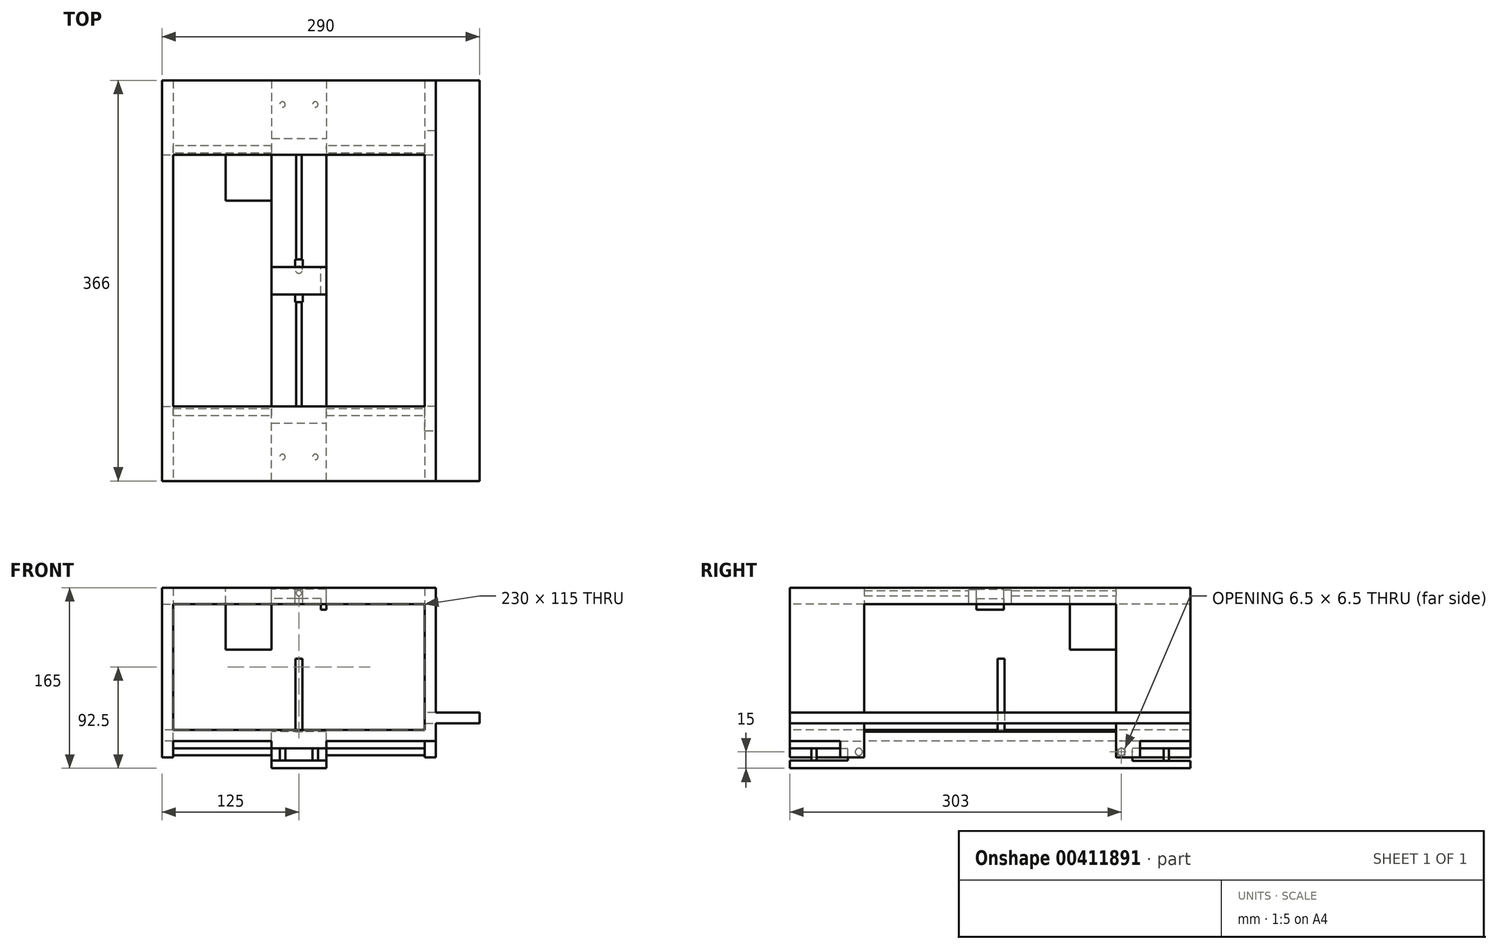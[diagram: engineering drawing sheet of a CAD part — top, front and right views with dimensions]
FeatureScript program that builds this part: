
annotation { "Feature Type Name" : "Feature", "Feature Type Description" : "" }
export const myFeature = defineFeature(function(context is Context, id is Id, definition is map)
    precondition{}
    {
        {
            var Q0;
            Q0=qCreatedBy(makeId("Top.planeOp"),FACE);
            var sketch = newSketch(context, id + "F0", { "sketchPlane" : qUnion([Q0])});
            skLineSegment(sketch, "E0.bottom", {"start": v(-125, 125) * mm, "end": v(125, 125) * mm});
            skLineSegment(sketch, "E0.top", {"start": v(-125, -125) * mm, "end": v(125, -125) * mm});
            skLineSegment(sketch, "E0.left", {"start": v(-125, 125) * mm, "end": v(-125, -125) * mm});
            skLineSegment(sketch, "E0.right", {"start": v(125, 125) * mm, "end": v(125, -125) * mm});
            skSolve(sketch);
        }
        {
            var Q0;
            Q0 = qSketchRegion(id + "F0", true);
            extrude(context, id + "F1", {"entities" : qUnion([Q0]), "endBound" : BoundingType.SYMMETRIC, "depth" : 140 * mm});
        }
        {
            var Q0;
            Q0=makeQuery(id+"F1.opExtrude","CAP_FACE",FACE,{"disambiguationData":[OSD([sQuery(id+"F0.wireOp",EDGE,"E0.bottom"),sQuery(id+"F0.wireOp",EDGE,"E0.top"),sQuery(id+"F0.wireOp",EDGE,"E0.left"),sQuery(id+"F0.wireOp",EDGE,"E0.right")])],"isStart":false});
            shell(context, id + "F2", {"entities" : qUnion([Q0]), "thickness" : 10 * mm});
        }
        {
            var Q0;
            Q0=makeQuery(id+"F1.opExtrude","SWEPT_FACE",FACE,{"disambiguationData":[OSD([sQuery(id+"F0.wireOp",EDGE,"E0.top")])]});
            var sketch = newSketch(context, id + "F3", { "sketchPlane" : qUnion([Q0])});
            skLineSegment(sketch, "E1.bottom", {"start": v(-115, 60) * mm, "end": v(115, 60) * mm});
            skLineSegment(sketch, "E1.top", {"start": v(-115, -60) * mm, "end": v(115, -60) * mm});
            skLineSegment(sketch, "E1.left", {"start": v(-115, 60) * mm, "end": v(-115, -60) * mm});
            skLineSegment(sketch, "E1.right", {"start": v(115, 60) * mm, "end": v(115, -60) * mm});
            skSolve(sketch);
        }
        {
            var Q0;
            Q0=makeQuery(id+"F3.imprint","IMPRINT",FACE,{"disambiguationData":[TD([[makeQuery(id+"F3.imprint","IMPRINT",EDGE,{"derivedFrom":sQuery(id+"F3.wireOp",EDGE,"E1.bottom")}),-1.0]])]});
            extrude(context, id + "F4", {"entities" : qUnion([Q0]), "operationType" : NewBodyOperationType.REMOVE, "oppositeDirection" : true, "depth" : 300 * mm});
        }
        {
            var Q0;
            Q0=makeQuery(id+"F1.opExtrude","SWEPT_FACE",FACE,{"disambiguationData":[OSD([sQuery(id+"F0.wireOp",EDGE,"E0.left")])]});
            var sketch = newSketch(context, id + "F5", { "sketchPlane" : qUnion([Q0])});
            skLineSegment(sketch, "E2.bottom", {"start": v(115, 60) * mm, "end": v(-115, 60) * mm});
            skLineSegment(sketch, "E2.top", {"start": v(115, -60) * mm, "end": v(-115, -60) * mm});
            skLineSegment(sketch, "E2.left", {"start": v(115, 60) * mm, "end": v(115, -60) * mm});
            skLineSegment(sketch, "E2.right", {"start": v(-115, 60) * mm, "end": v(-115, -60) * mm});
            skSolve(sketch);
        }
        {
            var Q0;
            Q0=makeQuery(id+"F5.imprint","IMPRINT",FACE,{"disambiguationData":[TD([[makeQuery(id+"F5.imprint","IMPRINT",EDGE,{"derivedFrom":sQuery(id+"F5.wireOp",EDGE,"E2.bottom")}),1.0]])]});
            extrude(context, id + "F6", {"entities" : qUnion([Q0]), "operationType" : NewBodyOperationType.REMOVE, "oppositeDirection" : true, "depth" : 300 * mm});
        }
        {
            var Q0;
            Q0=makeQuery(id+"F6.boolean.opBoolean","MERGE",FACE,{"derivedFrom":[makeQuery(id+"F4.boolean.opBoolean","MERGE",FACE,{"derivedFrom":[makeQuery(id+"F2.opShell","OFFSET_FACE",FACE,{"disambiguationData":[OSD([sQuery(id+"F0.wireOp",EDGE,"E0.bottom"),sQuery(id+"F0.wireOp",EDGE,"E0.top"),sQuery(id+"F0.wireOp",EDGE,"E0.left"),sQuery(id+"F0.wireOp",EDGE,"E0.right")])]}),makeQuery(id+"F4.opExtrude","SWEPT_FACE",FACE,{"disambiguationData":[OSD([sQuery(id+"F3.wireOp",EDGE,"E1.top")])]})]}),makeQuery(id+"F6.opExtrude","SWEPT_FACE",FACE,{"disambiguationData":[OSD([sQuery(id+"F5.wireOp",EDGE,"E2.top")])]})]});
            var sketch = newSketch(context, id + "F7", { "sketchPlane" : qUnion([Q0])});
            skLineSegment(sketch, "E3.bottom", {"start": v(-115, 115) * mm, "end": v(115, 115) * mm});
            skLineSegment(sketch, "E3.top", {"start": v(-115, -115) * mm, "end": v(115, -115) * mm});
            skLineSegment(sketch, "E3.left", {"start": v(-115, 115) * mm, "end": v(-115, -115) * mm});
            skLineSegment(sketch, "E3.right", {"start": v(115, 115) * mm, "end": v(115, -115) * mm});
            skSolve(sketch);
        }
        {
            var Q0;
            Q0=makeQuery(id+"F7.imprint","IMPRINT",FACE,{"disambiguationData":[TD([[makeQuery(id+"F7.imprint","IMPRINT",EDGE,{"derivedFrom":sQuery(id+"F7.wireOp",EDGE,"E3.bottom")}),-1.0]])]});
            extrude(context, id + "F8", {"entities" : qUnion([Q0]), "operationType" : NewBodyOperationType.REMOVE, "oppositeDirection" : true, "depth" : 500 * mm});
        }
        {
            var Q0;
            Q0=makeQuery(id+"F1.opExtrude","CAP_FACE",FACE,{"disambiguationData":[OSD([sQuery(id+"F0.wireOp",EDGE,"E0.bottom"),sQuery(id+"F0.wireOp",EDGE,"E0.top"),sQuery(id+"F0.wireOp",EDGE,"E0.left"),sQuery(id+"F0.wireOp",EDGE,"E0.right")])],"isStart":true});
            var sketch = newSketch(context, id + "F9", { "sketchPlane" : qUnion([Q0])});
            skLineSegment(sketch, "E4.bottom", {"start": v(-125, -125) * mm, "end": v(-115, -125) * mm});
            skLineSegment(sketch, "E4.top", {"start": v(-125, -115) * mm, "end": v(-115, -115) * mm});
            skLineSegment(sketch, "E4.left", {"start": v(-125, -125) * mm, "end": v(-125, -115) * mm});
            skLineSegment(sketch, "E4.right", {"start": v(-115, -125) * mm, "end": v(-115, -115) * mm});
            skLineSegment(sketch, "E5.bottom", {"start": v(-115, 115) * mm, "end": v(-125, 115) * mm});
            skLineSegment(sketch, "E5.top", {"start": v(-115, 125) * mm, "end": v(-125, 125) * mm});
            skLineSegment(sketch, "E5.left", {"start": v(-115, 115) * mm, "end": v(-115, 125) * mm});
            skLineSegment(sketch, "E5.right", {"start": v(-125, 115) * mm, "end": v(-125, 125) * mm});
            skLineSegment(sketch, "E6.bottom", {"start": v(125, -125) * mm, "end": v(115, -125) * mm});
            skLineSegment(sketch, "E6.top", {"start": v(125, -115) * mm, "end": v(115, -115) * mm});
            skLineSegment(sketch, "E6.left", {"start": v(125, -125) * mm, "end": v(125, -115) * mm});
            skLineSegment(sketch, "E6.right", {"start": v(115, -125) * mm, "end": v(115, -115) * mm});
            skLineSegment(sketch, "E7.bottom", {"start": v(125, 125) * mm, "end": v(115, 125) * mm});
            skLineSegment(sketch, "E7.top", {"start": v(125, 115) * mm, "end": v(115, 115) * mm});
            skLineSegment(sketch, "E7.left", {"start": v(125, 125) * mm, "end": v(125, 115) * mm});
            skLineSegment(sketch, "E7.right", {"start": v(115, 125) * mm, "end": v(115, 115) * mm});
            skSolve(sketch);
        }
        {
            var Q0;
            Q0 = qSketchRegion(id + "F9", true);
            var Q1;
            Q1=makeQuery(id+"F1.opExtrude","CAP_FACE",FACE,{"disambiguationData":[OSD([sQuery(id+"F0.wireOp",EDGE,"E0.bottom"),sQuery(id+"F0.wireOp",EDGE,"E0.top"),sQuery(id+"F0.wireOp",EDGE,"E0.left"),sQuery(id+"F0.wireOp",EDGE,"E0.right")])],"isStart":false});
            extrude(context, id + "F10", {"entities" : qUnion([Q0, Q1]), "operationType" : NewBodyOperationType.ADD, "depth" : 15 * mm});
        }
        {
            var Q0;
            Q0=makeQuery(id+"F10.boolean.opBoolean","MERGE",FACE,{"derivedFrom":[makeQuery(id+"F1.opExtrude","SWEPT_FACE",FACE,{"disambiguationData":[OSD([sQuery(id+"F0.wireOp",EDGE,"E0.bottom")])]}),makeQuery(id+"F10.opExtrude","SWEPT_FACE",FACE,{"disambiguationData":[OSD([sQuery(id+"F9.wireOp",EDGE,"E4.bottom")])]}),makeQuery(id+"F10.opExtrude","SWEPT_FACE",FACE,{"disambiguationData":[OSD([sQuery(id+"F9.wireOp",EDGE,"E6.bottom")])]})]});
            var sketch = newSketch(context, id + "F11", { "sketchPlane" : qUnion([Q0])});
            skCircle(sketch, "E8", {"center": v(0, 65) * mm, "radius": 2.5 * mm});
            skSolve(sketch);
        }
        {
            var Q0;
            Q0 = qSketchRegion(id + "F11", true);
            extrude(context, id + "F12", {"entities" : qUnion([Q0]), "operationType" : NewBodyOperationType.ADD, "oppositeDirection" : true, "depth" : 250 * mm});
        }
        {
            var Q0;
            Q0=qCreatedBy(makeId("Front.planeOp"),FACE);
            var sketch = newSketch(context, id + "F13", { "sketchPlane" : qUnion([Q0])});
            skLineSegment(sketch, "E9.bottom", {"start": v(25, 50) * mm, "end": v(-25, 50) * mm});
            skLineSegment(sketch, "E9.top", {"start": v(25, 68.5) * mm, "end": v(-25, 68.5) * mm});
            skLineSegment(sketch, "E9.left", {"start": v(25, 50) * mm, "end": v(25, 68.5) * mm});
            skLineSegment(sketch, "E9.right", {"start": v(-25, 50) * mm, "end": v(-25, 68.5) * mm});
            skSolve(sketch);
        }
        {
            var Q0;
            Q0 = qSketchRegion(id + "F13", true);
            extrude(context, id + "F14", {"entities" : qUnion([Q0]), "operationType" : NewBodyOperationType.ADD, "endBound" : BoundingType.SYMMETRIC, "depth" : 25 * mm});
        }
        {
            var Q0;
            Q0=makeQuery(id+"F14.opExtrude","SWEPT_FACE",FACE,{"disambiguationData":[OSD([sQuery(id+"F13.wireOp",EDGE,"E9.bottom")])]});
            var sketch = newSketch(context, id + "F15", { "sketchPlane" : qUnion([Q0])});
            skLineSegment(sketch, "E10.right", {"start": v(20, 7.5) * mm, "end": v(20, -12.5) * mm});
            skLineSegment(sketch, "E11", {"start": v(20, 7.5) * mm, "end": v(20, 12.5) * mm});
            skLineSegment(sketch, "E12", {"start": v(20, 12.5) * mm, "end": v(25, 12.5) * mm});
            skLineSegment(sketch, "E13", {"start": v(25, 12.5) * mm, "end": v(25, -12.5) * mm});
            skLineSegment(sketch, "E14", {"start": v(25, -12.5) * mm, "end": v(20, -12.5) * mm});
            skSolve(sketch);
        }
        {
            var Q0;
            {var subQ3=sQuery(id+"F15.wireOp",EDGE,"E10.right");Q0=makeQuery(id+"F15.imprint","IMPRINT",FACE,{"disambiguationData":[TD([[makeQuery(id+"F15.imprint","IMPRINT",EDGE,{"derivedFrom":subQ3}),-1.0]])]});}
            extrude(context, id + "F16", {"entities" : qUnion([Q0]), "operationType" : NewBodyOperationType.REMOVE, "oppositeDirection" : true, "depth" : 10 * mm});
        }
        {
            var Q0;
            Q0=qCreatedBy(makeId("Right.planeOp"),FACE);
            var sketch = newSketch(context, id + "F17", { "sketchPlane" : qUnion([Q0])});
            skLineSegment(sketch, "E15.bottom", {"start": v(-12.5, 55) * mm, "end": v(-19.5, 55) * mm});
            skLineSegment(sketch, "E15.top", {"start": v(-12.5, 68) * mm, "end": v(-19.5, 68) * mm});
            skLineSegment(sketch, "E15.left", {"start": v(-12.5, 55) * mm, "end": v(-12.5, 68) * mm});
            skLineSegment(sketch, "E15.right", {"start": v(-19.5, 55) * mm, "end": v(-19.5, 68) * mm});
            skLineSegment(sketch, "E16.bottom", {"start": v(12.5, 55) * mm, "end": v(19.5, 55) * mm});
            skLineSegment(sketch, "E16.top", {"start": v(12.5, 68) * mm, "end": v(19.5, 68) * mm});
            skLineSegment(sketch, "E16.left", {"start": v(12.5, 55) * mm, "end": v(12.5, 68) * mm});
            skLineSegment(sketch, "E16.right", {"start": v(19.5, 55) * mm, "end": v(19.5, 68) * mm});
            skSolve(sketch);
        }
        {
            var Q0;
            Q0 = qSketchRegion(id + "F17", true);
            extrude(context, id + "F18", {"entities" : qUnion([Q0]), "operationType" : NewBodyOperationType.ADD, "endBound" : BoundingType.SYMMETRIC, "depth" : 7 * mm});
        }
        {
            var Q0;
            Q0=makeQuery(id+"F10.opExtrude","SWEPT_FACE",FACE,{"disambiguationData":[OSD([sQuery(id+"F9.wireOp",EDGE,"E4.right")])]});
            var sketch = newSketch(context, id + "F19", { "sketchPlane" : qUnion([Q0])});
            skCircle(sketch, "E17", {"center": v(120, -80) * mm, "radius": 3.25 * mm});
            skSolve(sketch);
        }
        {
            var Q0;
            Q0 = qSketchRegion(id + "F19", true);
            extrude(context, id + "F20", {"entities" : qUnion([Q0]), "operationType" : NewBodyOperationType.ADD, "depth" : 240 * mm});
        }
        {
            var Q0;
            Q0=qCreatedBy(makeId("Front.planeOp"),FACE);
            var sketch = newSketch(context, id + "F21", { "sketchPlane" : qUnion([Q0])});
            skLineSegment(sketch, "E18.bottom", {"start": v(25, -95) * mm, "end": v(-25, -95) * mm});
            skLineSegment(sketch, "E18.top", {"start": v(25, -61.69) * mm, "end": v(-25, -61.69) * mm});
            skLineSegment(sketch, "E18.left", {"start": v(25, -95) * mm, "end": v(25, -61.69) * mm});
            skLineSegment(sketch, "E18.right", {"start": v(-25, -95) * mm, "end": v(-25, -61.69) * mm});
            skSolve(sketch);
        }
        {
            var Q0;
            Q0=makeQuery(id+"F21.imprint","IMPRINT",FACE,{"disambiguationData":[TD([[makeQuery(id+"F21.imprint","IMPRINT",EDGE,{"derivedFrom":sQuery(id+"F21.wireOp",EDGE,"E18.bottom")}),-1.0]])]});
            extrude(context, id + "F22", {"entities" : qUnion([Q0]), "operationType" : NewBodyOperationType.ADD, "endBound" : BoundingType.SYMMETRIC, "depth" : 230 * mm});
        }
        {
            var Q0;
            Q0=makeQuery(id+"F10.opExtrude","SWEPT_FACE",FACE,{"disambiguationData":[OSD([sQuery(id+"F9.wireOp",EDGE,"E7.right")])]});
            var sketch = newSketch(context, id + "F23", { "sketchPlane" : qUnion([Q0])});
            skCircle(sketch, "E19", {"center": v(120, -80) * mm, "radius": 3.25 * mm});
            skSolve(sketch);
        }
        {
            var Q0;
            Q0=makeQuery(id+"F23.imprint","IMPRINT",FACE,{"disambiguationData":[TD([[makeQuery(id+"F23.imprint","IMPRINT",EDGE,{"derivedFrom":sQuery(id+"F23.wireOp",EDGE,"E19")}),1.0]])]});
            extrude(context, id + "F24", {"entities" : qUnion([Q0]), "operationType" : NewBodyOperationType.ADD, "depth" : 240 * mm});
        }
        {
            var Q0;
            Q0=makeQuery(id+"F22.opExtrude","SWEPT_FACE",FACE,{"disambiguationData":[OSD([sQuery(id+"F21.wireOp",EDGE,"E18.bottom")])]});
            var sketch = newSketch(context, id + "F25", { "sketchPlane" : qUnion([Q0])});
            skCircle(sketch, "E20", {"center": v(0, -10) * mm, "radius": 3.25 * mm});
            skSolve(sketch);
        }
        {
            var Q0;
            Q0=makeQuery(id+"F25.imprint","IMPRINT",FACE,{"disambiguationData":[TD([[makeQuery(id+"F25.imprint","IMPRINT",EDGE,{"derivedFrom":sQuery(id+"F25.wireOp",EDGE,"E20")}),1.0]])]});
            extrude(context, id + "F26", {"entities" : qUnion([Q0]), "operationType" : NewBodyOperationType.ADD, "oppositeDirection" : true, "depth" : 100 * mm});
        }
        {
            var Q0;
            Q0=makeQuery(id+"F1.opExtrude","CAP_FACE",FACE,{"disambiguationData":[OSD([sQuery(id+"F0.wireOp",EDGE,"E0.bottom"),sQuery(id+"F0.wireOp",EDGE,"E0.top"),sQuery(id+"F0.wireOp",EDGE,"E0.left"),sQuery(id+"F0.wireOp",EDGE,"E0.right")])],"isStart":false});
            var sketch = newSketch(context, id + "F27", { "sketchPlane" : qUnion([Q0])});
            skLineSegment(sketch, "E21.0", {"start": v(-25, -12.5) * mm, "end": v(-25, 12.5) * mm});
            skLineSegment(sketch, "E22.0", {"start": v(-25, -115) * mm, "end": v(-25, 115) * mm});
            skLineSegment(sketch, "E23.bottom", {"start": v(-25, 115) * mm, "end": v(-67, 115) * mm});
            skLineSegment(sketch, "E23.top", {"start": v(-25, 73) * mm, "end": v(-67, 73) * mm});
            skLineSegment(sketch, "E23.left", {"start": v(-25, 115) * mm, "end": v(-25, 73) * mm});
            skLineSegment(sketch, "E23.right", {"start": v(-67, 115) * mm, "end": v(-67, 73) * mm});
            skSolve(sketch);
        }
        {
            var Q0;
            Q0=makeQuery(id+"F27.imprint","IMPRINT",FACE,{"disambiguationData":[TD([[makeQuery(id+"F27.imprint","IMPRINT",EDGE,{"derivedFrom":sQuery(id+"F27.wireOp",EDGE,"E23.bottom")}),-1.0]])]});
            extrude(context, id + "F28", {"entities" : qUnion([Q0]), "oppositeDirection" : true, "depth" : 56.5 * mm});
        }
        {
            var Q0;
            {var subQ0=sQuery(id+"F0.wireOp",EDGE,"E0.bottom");Q0=makeQuery(id+"F10.boolean.opBoolean","MERGE",FACE,{"derivedFrom":[makeQuery(id+"F1.opExtrude","SWEPT_FACE",FACE,{"disambiguationData":[OSD([subQ0])]}),makeQuery(id+"F10.opExtrude","SWEPT_FACE",FACE,{"disambiguationData":[OSD([subQ0]),TDD([makeQuery(id+"F1.opExtrude","CAP_EDGE",EDGE,{"disambiguationData":[OSD([subQ0])],"isStart":false})])]}),makeQuery(id+"F10.opExtrude","SWEPT_FACE",FACE,{"disambiguationData":[OSD([sQuery(id+"F9.wireOp",EDGE,"E4.bottom")])]}),makeQuery(id+"F10.opExtrude","SWEPT_FACE",FACE,{"disambiguationData":[OSD([sQuery(id+"F9.wireOp",EDGE,"E6.bottom")])]})]});}
            var sketch = newSketch(context, id + "F29", { "sketchPlane" : qUnion([Q0])});
            skLineSegment(sketch, "E24.0.0", {"start": v(-115, -70) * mm, "end": v(115, -70) * mm});
            skLineSegment(sketch, "E24.0.1", {"start": v(115, -70) * mm, "end": v(115, -85) * mm});
            skLineSegment(sketch, "E24.0.2", {"start": v(115, -85) * mm, "end": v(125, -85) * mm});
            skLineSegment(sketch, "E24.0.3", {"start": v(125, -85) * mm, "end": v(125, 70) * mm});
            skLineSegment(sketch, "E24.0.4", {"start": v(125, 70) * mm, "end": v(-125, 70) * mm});
            skLineSegment(sketch, "E24.0.5", {"start": v(-125, 70) * mm, "end": v(-125, -85) * mm});
            skLineSegment(sketch, "E24.0.6", {"start": v(-125, -85) * mm, "end": v(-115, -85) * mm});
            skLineSegment(sketch, "E24.0.7", {"start": v(-115, -85) * mm, "end": v(-115, -70) * mm});
            skSolve(sketch);
        }
        {
            var Q0;
            Q0=makeQuery(id+"F29.imprint","IMPRINT",FACE,{"disambiguationData":[TD([[makeQuery(id+"F29.imprint","IMPRINT",EDGE,{"derivedFrom":sQuery(id+"F29.wireOp",EDGE,"E24.0.0")}),-1.0]])]});
            extrude(context, id + "F30", {"entities" : qUnion([Q0]), "operationType" : NewBodyOperationType.ADD, "depth" : 58 * mm});
        }
        {
            var Q0;
            {var subQ0=sQuery(id+"F0.wireOp",EDGE,"E0.top");Q0=makeQuery(id+"F10.boolean.opBoolean","MERGE",FACE,{"derivedFrom":[makeQuery(id+"F1.opExtrude","SWEPT_FACE",FACE,{"disambiguationData":[OSD([subQ0])]}),makeQuery(id+"F10.opExtrude","SWEPT_FACE",FACE,{"disambiguationData":[OSD([subQ0]),TDD([makeQuery(id+"F1.opExtrude","CAP_EDGE",EDGE,{"disambiguationData":[OSD([subQ0])],"isStart":false})])]}),makeQuery(id+"F10.opExtrude","SWEPT_FACE",FACE,{"disambiguationData":[OSD([sQuery(id+"F9.wireOp",EDGE,"E5.top")])]}),makeQuery(id+"F10.opExtrude","SWEPT_FACE",FACE,{"disambiguationData":[OSD([sQuery(id+"F9.wireOp",EDGE,"E7.bottom")])]})]});}
            var sketch = newSketch(context, id + "F31", { "sketchPlane" : qUnion([Q0])});
            skPoint(sketch, "E25.0", {"position": v(115, -70) * mm});
            skPoint(sketch, "E25.1", {"position": v(115, -60) * mm});
            skSolve(sketch);
        }
        {
            var Q0;
            {var subQ0=sQuery(id+"F0.wireOp",EDGE,"E0.top");var subQ3=makeQuery(id+"F1.opExtrude","CAP_EDGE",EDGE,{"disambiguationData":[OSD([subQ0])],"isStart":false});Q0=makeQuery(id+"F31.imprint","IMPRINT",FACE,{"disambiguationData":[TD([[makeQuery(id+"F31.imprint","IMPRINT",EDGE,{"derivedFrom":subQ3}),-1.0]])]});}
            extrude(context, id + "F32", {"entities" : qUnion([Q0]), "operationType" : NewBodyOperationType.ADD, "depth" : 58 * mm});
        }
        {
            var Q0;
            {var subQ0=sQuery(id+"F21.wireOp",EDGE,"E18.bottom");var subQ1=sQuery(id+"F21.wireOp",EDGE,"E18.left");var subQ2=sQuery(id+"F21.wireOp",EDGE,"E18.right");Q0=makeQuery(id+"F22.boolean.opBoolean","SPLIT",FACE,{"disambiguationData":[TD([makeQuery(id+"F22.opExtrude","SWEPT_FACE",FACE,{"disambiguationData":[OSD([subQ0])]})])],"derivedFrom":makeQuery(id+"F22.opExtrude","CAP_FACE",FACE,{"disambiguationData":[OSD([subQ0,sQuery(id+"F21.wireOp",EDGE,"E18.top"),subQ1,subQ2])],"isStart":true})});}
            var sketch = newSketch(context, id + "F33", { "sketchPlane" : qUnion([Q0])});
            skLineSegment(sketch, "E26.0.0", {"start": v(25, -95) * mm, "end": v(25, -70) * mm});
            skLineSegment(sketch, "E26.0.1", {"start": v(25, -70) * mm, "end": v(-25, -70) * mm});
            skLineSegment(sketch, "E26.0.2", {"start": v(-25, -70) * mm, "end": v(-25, -95) * mm});
            skLineSegment(sketch, "E26.0.3", {"start": v(-25, -95) * mm, "end": v(25, -95) * mm});
            skSolve(sketch);
        }
        {
            var Q0;
            Q0 = qSketchRegion(id + "F33", true);
            extrude(context, id + "F34", {"entities" : qUnion([Q0]), "operationType" : NewBodyOperationType.ADD, "depth" : 15 * mm});
        }
        {
            var Q0;
            Q0=makeQuery(id+"F34.opExtrude","CAP_FACE",FACE,{"disambiguationData":[OSD([sQuery(id+"F33.wireOp",EDGE,"E26.0.0"),sQuery(id+"F33.wireOp",EDGE,"E26.0.1"),sQuery(id+"F33.wireOp",EDGE,"E26.0.2"),sQuery(id+"F33.wireOp",EDGE,"E26.0.3")])],"isStart":false});
            var sketch = newSketch(context, id + "F35", { "sketchPlane" : qUnion([Q0])});
            skLineSegment(sketch, "E27.bottom", {"start": v(25, -95) * mm, "end": v(-25, -95) * mm});
            skLineSegment(sketch, "E27.top", {"start": v(25, -88.07) * mm, "end": v(-25, -88.07) * mm});
            skLineSegment(sketch, "E27.left", {"start": v(25, -95) * mm, "end": v(25, -88.07) * mm});
            skLineSegment(sketch, "E27.right", {"start": v(-25, -95) * mm, "end": v(-25, -88.07) * mm});
            skLineSegment(sketch, "E28.bottom", {"start": v(25, -70) * mm, "end": v(-25, -70) * mm});
            skLineSegment(sketch, "E28.top", {"start": v(25, -76.65) * mm, "end": v(-25, -76.65) * mm});
            skLineSegment(sketch, "E28.left", {"start": v(25, -70) * mm, "end": v(25, -76.65) * mm});
            skLineSegment(sketch, "E28.right", {"start": v(-25, -70) * mm, "end": v(-25, -76.65) * mm});
            skSolve(sketch);
        }
        {
            var Q0;
            Q0=makeQuery(id+"F35.imprint","IMPRINT",FACE,{"disambiguationData":[TD([[makeQuery(id+"F35.imprint","IMPRINT",EDGE,{"derivedFrom":sQuery(id+"F35.wireOp",EDGE,"E27.bottom")}),1.0]])]});
            var Q1;
            Q1=makeQuery(id+"F35.imprint","IMPRINT",FACE,{"disambiguationData":[TD([[makeQuery(id+"F35.imprint","IMPRINT",EDGE,{"derivedFrom":sQuery(id+"F35.wireOp",EDGE,"E28.bottom")}),1.0]])]});
            var Q2;
            Q2=makeQuery(id+"F30.opExtrude","CAP_FACE",FACE,{"disambiguationData":[OSD([sQuery(id+"F0.wireOp",EDGE,"E0.bottom"),sQuery(id+"F3.wireOp",EDGE,"E1.top"),sQuery(id+"F3.wireOp",EDGE,"E1.left"),sQuery(id+"F3.wireOp",EDGE,"E1.right"),sQuery(id+"F29.wireOp",EDGE,"E24.0.0"),sQuery(id+"F29.wireOp",EDGE,"E24.0.1"),sQuery(id+"F29.wireOp",EDGE,"E24.0.2"),sQuery(id+"F29.wireOp",EDGE,"E24.0.3"),sQuery(id+"F29.wireOp",EDGE,"E24.0.4"),sQuery(id+"F29.wireOp",EDGE,"E24.0.5"),sQuery(id+"F29.wireOp",EDGE,"E24.0.6"),sQuery(id+"F29.wireOp",EDGE,"E24.0.7")])],"isStart":false});
            extrude(context, id + "F36", {"entities" : qUnion([Q0, Q1]), "operationType" : NewBodyOperationType.ADD, "endBound" : BoundingType.UP_TO_SURFACE, "endBoundEntityFace" : qUnion([Q2]), "depth" : 25 * mm});
        }
        {
            var Q0;
            Q0=makeQuery(id+"F36.opExtrude","SWEPT_FACE",FACE,{"disambiguationData":[OSD([sQuery(id+"F35.wireOp",EDGE,"E28.top")])]});
            var sketch = newSketch(context, id + "F37", { "sketchPlane" : qUnion([Q0])});
            skCircle(sketch, "E29", {"center": v(-15, -161) * mm, "radius": 2.5 * mm});
            skCircle(sketch, "E30", {"center": v(15, -161) * mm, "radius": 2.5 * mm});
            skSolve(sketch);
        }
        {
            var Q0;
            Q0=makeQuery(id+"F37.imprint","IMPRINT",FACE,{"disambiguationData":[TD([[makeQuery(id+"F37.imprint","IMPRINT",EDGE,{"derivedFrom":sQuery(id+"F37.wireOp",EDGE,"E29")}),1.0]])]});
            var Q1;
            Q1=makeQuery(id+"F37.imprint","IMPRINT",FACE,{"disambiguationData":[TD([[makeQuery(id+"F37.imprint","IMPRINT",EDGE,{"derivedFrom":sQuery(id+"F37.wireOp",EDGE,"E30")}),1.0]])]});
            extrude(context, id + "F38", {"entities" : qUnion([Q0, Q1]), "operationType" : NewBodyOperationType.ADD, "endBound" : BoundingType.UP_TO_NEXT, "depth" : 25 * mm});
        }
        {
            var Q0;
            {var subQ0=sQuery(id+"F0.wireOp",EDGE,"E0.right");var subQ1=makeQuery(id+"F1.opExtrude","CAP_FACE",FACE,{"disambiguationData":[OSD([sQuery(id+"F0.wireOp",EDGE,"E0.bottom"),sQuery(id+"F0.wireOp",EDGE,"E0.top"),sQuery(id+"F0.wireOp",EDGE,"E0.left"),subQ0])],"isStart":true});Q0=makeQuery(id+"F10.boolean.opBoolean","SPLIT",FACE,{"disambiguationData":[TD([makeQuery(id+"F1.opExtrude","SWEPT_FACE",FACE,{"disambiguationData":[OSD([subQ0])]})])],"derivedFrom":subQ1});}
            var sketch = newSketch(context, id + "F39", { "sketchPlane" : qUnion([Q0])});
            skLineSegment(sketch, "E31.bottom", {"start": v(115, -115) * mm, "end": v(125, -115) * mm});
            skLineSegment(sketch, "E31.top", {"start": v(115, 115) * mm, "end": v(125, 115) * mm});
            skLineSegment(sketch, "E31.left", {"start": v(115, -115) * mm, "end": v(115, 115) * mm});
            skLineSegment(sketch, "E31.right", {"start": v(125, -115) * mm, "end": v(125, 115) * mm});
            skSolve(sketch);
        }
        {
            var Q0;
            Q0=makeQuery(id+"F39.imprint","IMPRINT",FACE,{"disambiguationData":[TD([[makeQuery(id+"F39.imprint","IMPRINT",EDGE,{"derivedFrom":sQuery(id+"F39.wireOp",EDGE,"E31.bottom")}),-1.0]])]});
            extrude(context, id + "F40", {"entities" : qUnion([Q0]), "operationType" : NewBodyOperationType.REMOVE, "oppositeDirection" : true, "depth" : 25 * mm});
        }
        {
            var Q0;
            {var subQ0=sQuery(id+"F0.wireOp",EDGE,"E0.right");Q0=makeQuery(id+"F40.boolean.opBoolean","MERGE",FACE,{"derivedFrom":[makeQuery(id+"F10.opExtrude","SWEPT_FACE",FACE,{"disambiguationData":[OSD([sQuery(id+"F9.wireOp",EDGE,"E6.top")])]}),makeQuery(id+"F6.boolean.opBoolean","COPY",FACE,{"disambiguationData":[TD([makeQuery(id+"F1.opExtrude","SWEPT_FACE",FACE,{"disambiguationData":[OSD([subQ0])]})])],"derivedFrom":makeQuery(id+"F6.opExtrude","SWEPT_FACE",FACE,{"disambiguationData":[OSD([sQuery(id+"F5.wireOp",EDGE,"E2.right")])]})}),makeQuery(id+"F8.boolean.opBoolean","COPY",FACE,{"derivedFrom":makeQuery(id+"F8.opExtrude","SWEPT_FACE",FACE,{"disambiguationData":[OSD([sQuery(id+"F7.wireOp",EDGE,"E3.bottom")])]})}),makeQuery(id+"F40.opExtrude","SWEPT_FACE",FACE,{"disambiguationData":[OSD([sQuery(id+"F39.wireOp",EDGE,"E31.bottom")])]})]});}
            var sketch = newSketch(context, id + "F41", { "sketchPlane" : qUnion([Q0])});
            skLineSegment(sketch, "E32.bottom", {"start": v(115, -54) * mm, "end": v(165, -54) * mm});
            skLineSegment(sketch, "E32.top", {"start": v(115, -44) * mm, "end": v(165, -44) * mm});
            skLineSegment(sketch, "E32.left", {"start": v(115, -54) * mm, "end": v(115, -44) * mm});
            skLineSegment(sketch, "E32.right", {"start": v(165, -54) * mm, "end": v(165, -44) * mm});
            skSolve(sketch);
        }
        {
            var Q0;
            {var subQ0=sQuery(id+"F41.wireOp",EDGE,"E32.right");Q0=makeQuery(id+"F41.imprint","IMPRINT",FACE,{"disambiguationData":[TD([[makeQuery(id+"F41.imprint","IMPRINT",EDGE,{"derivedFrom":subQ0}),1.0]])]});}
            var Q1;
            {var subQ0=sQuery(id+"F41.wireOp",EDGE,"E32.left");Q1=makeQuery(id+"F41.imprint","IMPRINT",FACE,{"disambiguationData":[TD([[makeQuery(id+"F41.imprint","IMPRINT",EDGE,{"derivedFrom":subQ0}),-1.0]])]});}
            var Q2;
            {var subQ2=sQuery(id+"F0.wireOp",EDGE,"E0.right");Q2=makeQuery(id+"F40.boolean.opBoolean","MERGE",FACE,{"derivedFrom":[makeQuery(id+"F10.opExtrude","SWEPT_FACE",FACE,{"disambiguationData":[OSD([sQuery(id+"F9.wireOp",EDGE,"E7.top")])]}),makeQuery(id+"F6.boolean.opBoolean","COPY",FACE,{"disambiguationData":[TD([makeQuery(id+"F1.opExtrude","SWEPT_FACE",FACE,{"disambiguationData":[OSD([subQ2])]})])],"derivedFrom":makeQuery(id+"F6.opExtrude","SWEPT_FACE",FACE,{"disambiguationData":[OSD([sQuery(id+"F5.wireOp",EDGE,"E2.left")])]})}),makeQuery(id+"F8.boolean.opBoolean","COPY",FACE,{"derivedFrom":makeQuery(id+"F8.opExtrude","SWEPT_FACE",FACE,{"disambiguationData":[OSD([sQuery(id+"F7.wireOp",EDGE,"E3.top")])]})}),makeQuery(id+"F40.opExtrude","SWEPT_FACE",FACE,{"disambiguationData":[OSD([sQuery(id+"F39.wireOp",EDGE,"E31.top")])]})]});}
            extrude(context, id + "F42", {"entities" : qUnion([Q0, Q1]), "operationType" : NewBodyOperationType.ADD, "endBound" : BoundingType.UP_TO_SURFACE, "endBoundEntityFace" : qUnion([Q2]), "depth" : 211 * mm});
        }
        {
            var Q0;
            Q0=makeQuery(id+"F42.opExtrude","CAP_FACE",FACE,{"disambiguationData":[OSD([sQuery(id+"F41.wireOp",EDGE,"E32.bottom"),sQuery(id+"F41.wireOp",EDGE,"E32.top"),sQuery(id+"F41.wireOp",EDGE,"E32.left"),sQuery(id+"F41.wireOp",EDGE,"E32.right")])],"isStart":true});
            var sketch = newSketch(context, id + "F43", { "sketchPlane" : qUnion([Q0])});
            skLineSegment(sketch, "E33.bottom", {"start": v(-165, -54) * mm, "end": v(-125, -54) * mm});
            skLineSegment(sketch, "E33.top", {"start": v(-165, -44) * mm, "end": v(-125, -44) * mm});
            skLineSegment(sketch, "E33.left", {"start": v(-165, -54) * mm, "end": v(-165, -44) * mm});
            skLineSegment(sketch, "E33.right", {"start": v(-125, -54) * mm, "end": v(-125, -44) * mm});
            skSolve(sketch);
        }
        {
            var Q0;
            Q0=makeQuery(id+"F43.imprint","IMPRINT",FACE,{"disambiguationData":[TD([[makeQuery(id+"F43.imprint","IMPRINT",EDGE,{"derivedFrom":sQuery(id+"F43.wireOp",EDGE,"E33.bottom")}),-1.0]])]});
            var Q1;
            Q1=makeQuery(id+"F36.boolean.opBoolean","MERGE",FACE,{"derivedFrom":[makeQuery(id+"F30.opExtrude","CAP_FACE",FACE,{"disambiguationData":[OSD([sQuery(id+"F0.wireOp",EDGE,"E0.bottom"),sQuery(id+"F3.wireOp",EDGE,"E1.top"),sQuery(id+"F3.wireOp",EDGE,"E1.left"),sQuery(id+"F3.wireOp",EDGE,"E1.right"),sQuery(id+"F29.wireOp",EDGE,"E24.0.0"),sQuery(id+"F29.wireOp",EDGE,"E24.0.1"),sQuery(id+"F29.wireOp",EDGE,"E24.0.2"),sQuery(id+"F29.wireOp",EDGE,"E24.0.3"),sQuery(id+"F29.wireOp",EDGE,"E24.0.4"),sQuery(id+"F29.wireOp",EDGE,"E24.0.5"),sQuery(id+"F29.wireOp",EDGE,"E24.0.6"),sQuery(id+"F29.wireOp",EDGE,"E24.0.7")])],"isStart":false}),makeQuery(id+"F36.opExtrude","CAP_FACE",FACE,{"disambiguationData":[OSD([sQuery(id+"F35.wireOp",EDGE,"E28.bottom"),sQuery(id+"F35.wireOp",EDGE,"E28.top"),sQuery(id+"F35.wireOp",EDGE,"E28.left"),sQuery(id+"F35.wireOp",EDGE,"E28.right")])],"isStart":false})]});
            extrude(context, id + "F44", {"entities" : qUnion([Q0]), "operationType" : NewBodyOperationType.ADD, "endBound" : BoundingType.UP_TO_SURFACE, "endBoundEntityFace" : qUnion([Q1]), "depth" : 25 * mm});
        }
        {
            var Q0;
            Q0=makeQuery(id+"F30.boolean.opBoolean","MERGE",FACE,{"derivedFrom":[makeQuery(id+"F10.opExtrude","SWEPT_FACE",FACE,{"disambiguationData":[OSD([sQuery(id+"F9.wireOp",EDGE,"E6.right")])]}),makeQuery(id+"F30.opExtrude","SWEPT_FACE",FACE,{"disambiguationData":[OSD([sQuery(id+"F29.wireOp",EDGE,"E24.0.7")])]})]});
            var sketch = newSketch(context, id + "F45", { "sketchPlane" : qUnion([Q0])});
            skLineSegment(sketch, "E34.bottom", {"start": v(-183, -70) * mm, "end": v(-137.06, -70) * mm});
            skLineSegment(sketch, "E34.top", {"start": v(-183, -85) * mm, "end": v(-137.06, -85) * mm});
            skLineSegment(sketch, "E34.left", {"start": v(-183, -70) * mm, "end": v(-183, -85) * mm});
            skLineSegment(sketch, "E34.right", {"start": v(-137.06, -70) * mm, "end": v(-137.06, -85) * mm});
            skSolve(sketch);
        }
        {
            var Q0;
            Q0=makeQuery(id+"F45.imprint","IMPRINT",FACE,{"disambiguationData":[TD([[makeQuery(id+"F45.imprint","IMPRINT",EDGE,{"derivedFrom":sQuery(id+"F45.wireOp",EDGE,"E34.bottom")}),-1.0]])]});
            extrude(context, id + "F46", {"entities" : qUnion([Q0]), "operationType" : NewBodyOperationType.REMOVE, "oppositeDirection" : true, "depth" : 25 * mm});
        }
        {
            var Q0;
            Q0=makeQuery(id+"F42.opExtrude","CAP_FACE",FACE,{"disambiguationData":[OSD([sQuery(id+"F41.wireOp",EDGE,"E32.bottom"),sQuery(id+"F41.wireOp",EDGE,"E32.top"),sQuery(id+"F41.wireOp",EDGE,"E32.left"),sQuery(id+"F41.wireOp",EDGE,"E32.right")])],"isStart":false});
            var Q1;
            Q1=makeQuery(id+"F32.opExtrude","CAP_FACE",FACE,{"disambiguationData":[OSD([sQuery(id+"F0.wireOp",EDGE,"E0.top"),sQuery(id+"F0.wireOp",EDGE,"E0.left"),sQuery(id+"F0.wireOp",EDGE,"E0.right"),sQuery(id+"F3.wireOp",EDGE,"E1.top"),sQuery(id+"F3.wireOp",EDGE,"E1.left"),sQuery(id+"F3.wireOp",EDGE,"E1.right"),sQuery(id+"F9.wireOp",EDGE,"E5.top"),sQuery(id+"F9.wireOp",EDGE,"E5.left"),sQuery(id+"F9.wireOp",EDGE,"E5.right"),sQuery(id+"F9.wireOp",EDGE,"E7.bottom"),sQuery(id+"F9.wireOp",EDGE,"E7.left"),sQuery(id+"F9.wireOp",EDGE,"E7.right")])],"isStart":false});
            extrude(context, id + "F47", {"entities" : qUnion([Q0]), "operationType" : NewBodyOperationType.ADD, "endBound" : BoundingType.UP_TO_SURFACE, "endBoundEntityFace" : qUnion([Q1]), "depth" : 25 * mm});
        }
        {
            var Q0;
            {var subQ1=sQuery(id+"F29.wireOp",EDGE,"E24.0.6");var subQ2=sQuery(id+"F9.wireOp",EDGE,"E6.left");var subQ4=sQuery(id+"F0.wireOp",EDGE,"E0.right");var subQ6=sQuery(id+"F0.wireOp",EDGE,"E0.top");var subQ8=makeQuery(id+"F1.opExtrude","SWEPT_FACE",FACE,{"disambiguationData":[OSD([subQ4])]});var subQ13=sQuery(id+"F29.wireOp",EDGE,"E24.0.5");var subQ14=sQuery(id+"F9.wireOp",EDGE,"E7.left");Q0=makeQuery(id+"F44.boolean.opBoolean","SPLIT",FACE,{"disambiguationData":[TD([makeQuery(id+"F30.opExtrude","SWEPT_FACE",FACE,{"disambiguationData":[OSD([subQ1])]})])],"derivedFrom":makeQuery(id+"F32.boolean.opBoolean","MERGE",FACE,{"derivedFrom":[makeQuery(id+"F30.boolean.opBoolean","MERGE",FACE,{"derivedFrom":[makeQuery(id+"F10.boolean.opBoolean","MERGE",FACE,{"derivedFrom":[subQ8,makeQuery(id+"F10.opExtrude","SWEPT_FACE",FACE,{"disambiguationData":[OSD([subQ4]),TDD([makeQuery(id+"F1.opExtrude","CAP_EDGE",EDGE,{"disambiguationData":[OSD([subQ4])],"isStart":false})])]}),makeQuery(id+"F10.opExtrude","SWEPT_FACE",FACE,{"disambiguationData":[OSD([subQ2])]}),makeQuery(id+"F10.opExtrude","SWEPT_FACE",FACE,{"disambiguationData":[OSD([subQ14])]})]}),makeQuery(id+"F30.opExtrude","SWEPT_FACE",FACE,{"disambiguationData":[OSD([subQ13])]})]}),makeQuery(id+"F32.opExtrude","SWEPT_FACE",FACE,{"disambiguationData":[OSD([subQ6,subQ4,sQuery(id+"F9.wireOp",EDGE,"E7.bottom"),subQ14])]})]})});}
            var sketch = newSketch(context, id + "F48", { "sketchPlane" : qUnion([Q0])});
            skLineSegment(sketch, "E35.0", {"start": v(-115, -85) * mm, "end": v(-183, -85) * mm});
            skPoint(sketch, "E36.0", {"position": v(-115, -69.5) * mm});
            skLineSegment(sketch, "E37", {"start": v(-137.06, -85) * mm, "end": v(-137.06, -70) * mm});
            skLineSegment(sketch, "E38.0", {"start": v(137.06, -70) * mm, "end": v(183, -70) * mm});
            skLineSegment(sketch, "E39.0", {"start": v(137.06, -85) * mm, "end": v(115, -85) * mm});
            skLineSegment(sketch, "E40.0", {"start": v(115, -85) * mm, "end": v(115, -54) * mm});
            skLineSegment(sketch, "E41", {"start": v(-183, -85) * mm, "end": v(-183, -70) * mm});
            skLineSegment(sketch, "E42", {"start": v(-183, -70) * mm, "end": v(-137.06, -70) * mm});
            skSolve(sketch);
        }
        {
            var Q0;
            {var subQ2=sQuery(id+"F48.wireOp",EDGE,"E37");Q0=makeQuery(id+"F48.imprint","IMPRINT",FACE,{"disambiguationData":[TD([[makeQuery(id+"F48.imprint","IMPRINT",EDGE,{"derivedFrom":subQ2}),1.0]])]});}
            extrude(context, id + "F49", {"entities" : qUnion([Q0]), "operationType" : NewBodyOperationType.REMOVE, "oppositeDirection" : true, "depth" : 25 * mm});
        }
        {
            var Q0;
            Q0=makeQuery(id+"F22.opExtrude","CAP_FACE",FACE,{"disambiguationData":[OSD([sQuery(id+"F21.wireOp",EDGE,"E18.bottom"),sQuery(id+"F21.wireOp",EDGE,"E18.top"),sQuery(id+"F21.wireOp",EDGE,"E18.left"),sQuery(id+"F21.wireOp",EDGE,"E18.right")])],"isStart":false});
            var Q1;
            Q1=makeQuery(id+"F47.boolean.opBoolean","MERGE",FACE,{"derivedFrom":[makeQuery(id+"F32.opExtrude","CAP_FACE",FACE,{"disambiguationData":[OSD([sQuery(id+"F0.wireOp",EDGE,"E0.top"),sQuery(id+"F0.wireOp",EDGE,"E0.left"),sQuery(id+"F0.wireOp",EDGE,"E0.right"),sQuery(id+"F3.wireOp",EDGE,"E1.top"),sQuery(id+"F3.wireOp",EDGE,"E1.left"),sQuery(id+"F3.wireOp",EDGE,"E1.right"),sQuery(id+"F9.wireOp",EDGE,"E5.top"),sQuery(id+"F9.wireOp",EDGE,"E5.left"),sQuery(id+"F9.wireOp",EDGE,"E5.right"),sQuery(id+"F9.wireOp",EDGE,"E7.bottom"),sQuery(id+"F9.wireOp",EDGE,"E7.left"),sQuery(id+"F9.wireOp",EDGE,"E7.right")])],"isStart":false}),makeQuery(id+"F47.opExtrude","CAP_FACE",FACE,{"disambiguationData":[OSD([sQuery(id+"F41.wireOp",EDGE,"E32.bottom"),sQuery(id+"F41.wireOp",EDGE,"E32.top"),sQuery(id+"F41.wireOp",EDGE,"E32.left"),sQuery(id+"F41.wireOp",EDGE,"E32.right")])],"isStart":false})]});
            extrude(context, id + "F50", {"entities" : qUnion([Q0]), "operationType" : NewBodyOperationType.ADD, "endBound" : BoundingType.UP_TO_SURFACE, "endBoundEntityFace" : qUnion([Q1]), "depth" : 25 * mm});
        }
        {
            var Q0;
            {var subQ0=sQuery(id+"F21.wireOp",EDGE,"E18.left");Q0=makeQuery(id+"F50.boolean.opBoolean","MERGE",FACE,{"derivedFrom":[makeQuery(id+"F36.boolean.opBoolean","MERGE",FACE,{"derivedFrom":[makeQuery(id+"F34.boolean.opBoolean","MERGE",FACE,{"derivedFrom":[makeQuery(id+"F22.opExtrude","SWEPT_FACE",FACE,{"disambiguationData":[OSD([subQ0])]}),makeQuery(id+"F34.opExtrude","SWEPT_FACE",FACE,{"disambiguationData":[OSD([sQuery(id+"F33.wireOp",EDGE,"E26.0.2")])]})]}),makeQuery(id+"F36.opExtrude","SWEPT_FACE",FACE,{"disambiguationData":[OSD([sQuery(id+"F35.wireOp",EDGE,"E27.right")])]}),makeQuery(id+"F36.opExtrude","SWEPT_FACE",FACE,{"disambiguationData":[OSD([sQuery(id+"F35.wireOp",EDGE,"E28.right")])]})]}),makeQuery(id+"F50.opExtrude","SWEPT_FACE",FACE,{"disambiguationData":[OSD([subQ0])]})]});}
            var sketch = newSketch(context, id + "F51", { "sketchPlane" : qUnion([Q0])});
            skLineSegment(sketch, "E43.0", {"start": v(130, -88.07) * mm, "end": v(130, -76.65) * mm});
            skLineSegment(sketch, "E44.0", {"start": v(183, -95) * mm, "end": v(183, -88.07) * mm});
            skLineSegment(sketch, "E45.0", {"start": v(183, -76.65) * mm, "end": v(183, -70) * mm});
            skLineSegment(sketch, "E46.bottom", {"start": v(-183, -88) * mm, "end": v(-130, -88) * mm});
            skLineSegment(sketch, "E46.top", {"start": v(-183, -76.7) * mm, "end": v(-130, -76.7) * mm});
            skLineSegment(sketch, "E46.left", {"start": v(-183, -88) * mm, "end": v(-183, -76.7) * mm});
            skLineSegment(sketch, "E46.right", {"start": v(-130, -88) * mm, "end": v(-130, -76.7) * mm});
            skSolve(sketch);
        }
        {
            var Q0;
            Q0=makeQuery(id+"F51.imprint","IMPRINT",FACE,{"disambiguationData":[TD([[makeQuery(id+"F51.imprint","IMPRINT",EDGE,{"derivedFrom":sQuery(id+"F51.wireOp",EDGE,"E46.bottom")}),1.0]])]});
            extrude(context, id + "F52", {"entities" : qUnion([Q0]), "operationType" : NewBodyOperationType.REMOVE, "oppositeDirection" : true, "depth" : 50 * mm});
        }
        {
            var Q0;
            Q0=makeQuery(id+"F52.boolean.opBoolean","COPY",FACE,{"derivedFrom":makeQuery(id+"F52.opExtrude","SWEPT_FACE",FACE,{"disambiguationData":[OSD([sQuery(id+"F51.wireOp",EDGE,"E46.top")])]})});
            var sketch = newSketch(context, id + "F53", { "sketchPlane" : qUnion([Q0])});
            skCircle(sketch, "E47", {"center": v(15, 161) * mm, "radius": 2.5 * mm});
            skCircle(sketch, "E48", {"center": v(-15, 161) * mm, "radius": 2.5 * mm});
            skSolve(sketch);
        }
        {
            var Q0;
            Q0=makeQuery(id+"F53.imprint","IMPRINT",FACE,{"disambiguationData":[TD([[makeQuery(id+"F53.imprint","IMPRINT",EDGE,{"derivedFrom":sQuery(id+"F53.wireOp",EDGE,"E47")}),1.0]])]});
            var Q1;
            Q1=makeQuery(id+"F53.imprint","IMPRINT",FACE,{"disambiguationData":[TD([[makeQuery(id+"F53.imprint","IMPRINT",EDGE,{"derivedFrom":sQuery(id+"F53.wireOp",EDGE,"E48")}),1.0]])]});
            var Q2;
            {var subQ0=sQuery(id+"F21.wireOp",EDGE,"E18.bottom");Q2=makeQuery(id+"F50.boolean.opBoolean","MERGE",FACE,{"derivedFrom":[makeQuery(id+"F36.boolean.opBoolean","MERGE",FACE,{"derivedFrom":[makeQuery(id+"F34.boolean.opBoolean","MERGE",FACE,{"derivedFrom":[makeQuery(id+"F22.opExtrude","SWEPT_FACE",FACE,{"disambiguationData":[OSD([subQ0])]}),makeQuery(id+"F34.opExtrude","SWEPT_FACE",FACE,{"disambiguationData":[OSD([sQuery(id+"F33.wireOp",EDGE,"E26.0.3")])]})]}),makeQuery(id+"F36.opExtrude","SWEPT_FACE",FACE,{"disambiguationData":[OSD([sQuery(id+"F35.wireOp",EDGE,"E27.bottom")])]})]}),makeQuery(id+"F50.opExtrude","SWEPT_FACE",FACE,{"disambiguationData":[OSD([subQ0])]})]});}
            extrude(context, id + "F54", {"entities" : qUnion([Q0, Q1]), "operationType" : NewBodyOperationType.ADD, "endBound" : BoundingType.UP_TO_SURFACE, "endBoundEntityFace" : qUnion([Q2]), "depth" : 25 * mm});
        }
    });
